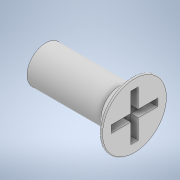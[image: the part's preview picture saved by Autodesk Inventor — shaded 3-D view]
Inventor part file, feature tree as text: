
AUTODESK INVENTOR PART (.ipt)
format: ipt  version: 2020 (Build 240168000, 168)  size: 142,336 bytes
history: native  units: mm
features: sketch x2, revolve x1, fillet x1, extrude x1, projected_geometry x1
ambient origin geometry x8: Origin, YZ Plane, XZ Plane, XY Plane, X Axis, Y Axis, Z Axis, Center Point
bodies: Solid1 (feature_tree)
feature tree (6):
  revolve  "Revolution1"  [1 undecoded]
  fillet  "Fillet1"  Radius=4.0mm
  extrude  "Extrusion1"  TaperAngle=90.0deg  [1 undecoded]
  sketch  "Sketch1"  dims[d0=1.85mm d1=0.8mm d2=4.0mm]
  sketch  "Sketch2"  dims[d3=1.0mm d4=90.0deg d5=0.05mm d6=0.4mm d7=2.5mm d8=0.4mm d9=2.5mm d10=0.4mm d11=0.0mm]
  projected_geometry  "Projected Loop1"
note: 2 required parameter values undecoded (feature->parameter linkage not recoverable at this tier; creation-order binding heuristic only, values carry confidence <= 0.55)